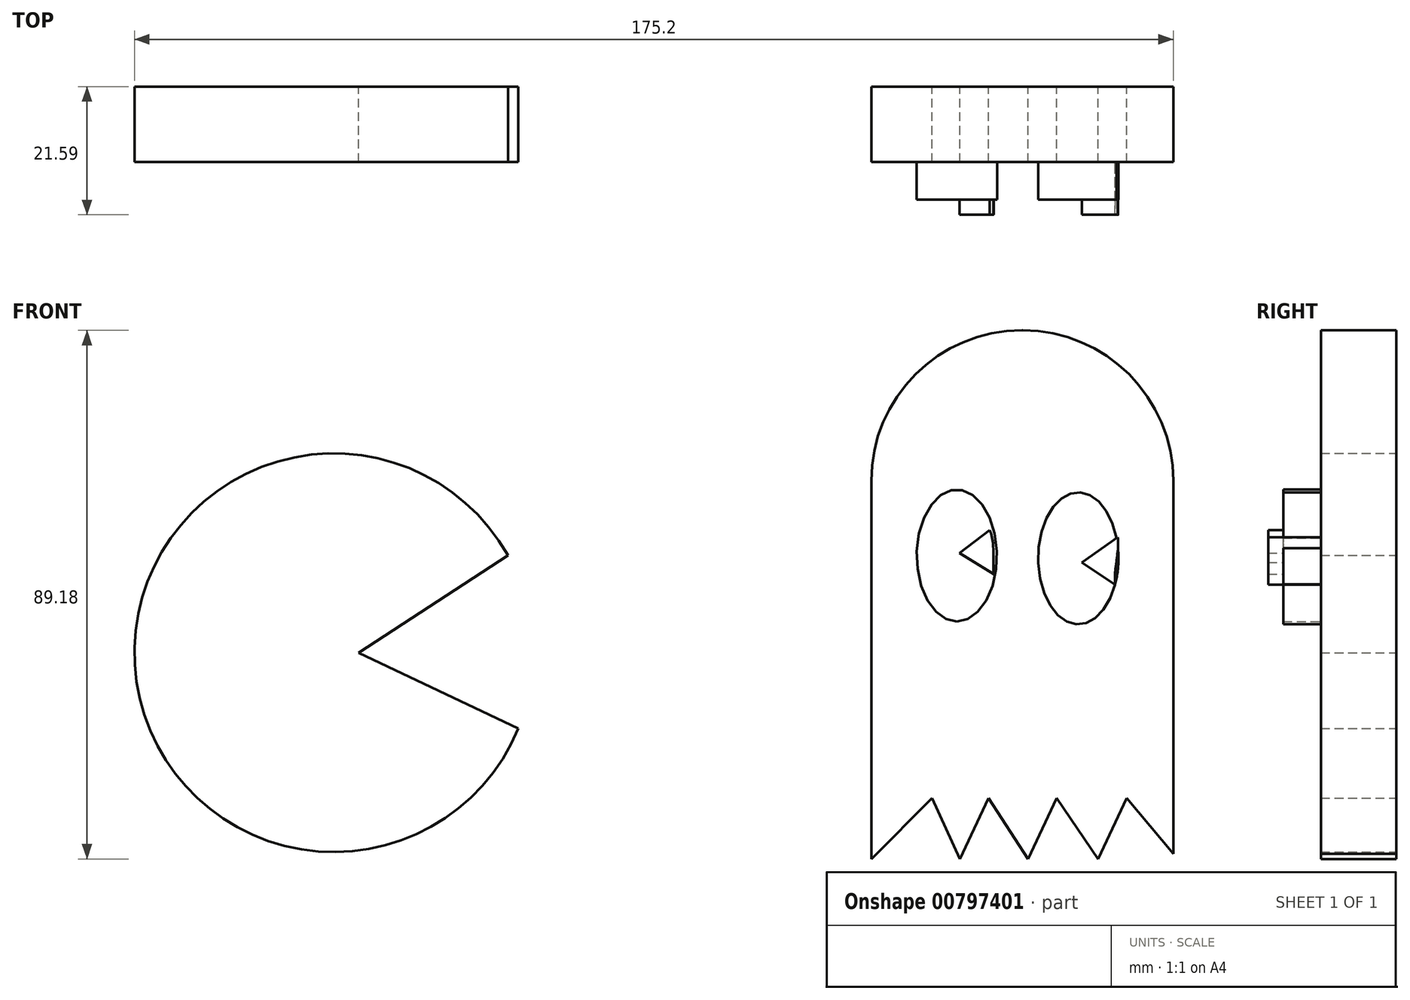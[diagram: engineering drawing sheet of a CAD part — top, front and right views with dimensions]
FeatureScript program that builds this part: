
annotation { "Feature Type Name" : "Feature", "Feature Type Description" : "" }
export const myFeature = defineFeature(function(context is Context, id is Id, definition is map)
    precondition{}
    {
        {
            var Q0;
            Q0=qCreatedBy(makeId("Front.planeOp"),FACE);
            var sketch = newSketch(context, id + "F0", { "sketchPlane" : qUnion([Q0])});
            skArc(sketch, "E0", {"start": v(-31.48, 14.91) * mm, "mid": v(-94.4, -3.54) * mm, "end": v(-29.71, -14.25) * mm});
            skLineSegment(sketch, "E1", {"start": v(-56.67, -1.5) * mm, "end": v(-31.48, 14.91) * mm});
            skLineSegment(sketch, "E2", {"start": v(-56.67, -1.5) * mm, "end": v(-29.71, -14.25) * mm});
            skLineSegment(sketch, "E3.bottom", {"start": v(55.2, 52.9) * mm, "end": v(55.34, 52.9) * mm});
            skLineSegment(sketch, "E3.left", {"start": v(29.8, 27.5) * mm, "end": v(29.8, -36.3) * mm});
            skLineSegment(sketch, "E3.right", {"start": v(80.74, 27.5) * mm, "end": v(80.74, -35.4) * mm});
            skPoint(sketch, "E4.visualSharp", {"position": v(29.8, 52.9) * mm});
            skArc(sketch, "E4.filletArc", {"start": v(33.93, 45.69) * mm, "mid": v(32.81, 44.12) * mm, "end": v(31.86, 42.45) * mm});
            skArc(sketch, "E5.filletArc", {"start": v(55.2, 52.9) * mm, "mid": v(37.24, 45.45) * mm, "end": v(29.8, 27.5) * mm});
            skPoint(sketch, "E6.visualSharp", {"position": v(80.74, 52.9) * mm});
            skArc(sketch, "E6.filletArc", {"start": v(72.07, 49.81) * mm, "mid": v(65.94, 52.4) * mm, "end": v(59.3, 52.74) * mm});
            skArc(sketch, "E7.filletArc", {"start": v(80.74, 27.5) * mm, "mid": v(73.3, 45.45) * mm, "end": v(55.34, 52.9) * mm});
            skLineSegment(sketch, "E8", {"start": v(29.8, -35.4) * mm, "end": v(29.8, -36.3) * mm});
            skLineSegment(sketch, "E9", {"start": v(80.74, -35.4) * mm, "end": v(80.74, -35.4) * mm});
            skLineSegment(sketch, "E10", {"start": v(29.8, -36.3) * mm, "end": v(40.03, -26.06) * mm});
            skLineSegment(sketch, "E11", {"start": v(40.03, -26.06) * mm, "end": v(44.74, -36.3) * mm});
            skLineSegment(sketch, "E12", {"start": v(44.74, -36.3) * mm, "end": v(49.58, -26.06) * mm});
            skLineSegment(sketch, "E13", {"start": v(49.58, -26.06) * mm, "end": v(56.25, -36.3) * mm});
            skLineSegment(sketch, "E14", {"start": v(56.25, -36.3) * mm, "end": v(61.1, -26.06) * mm});
            skLineSegment(sketch, "E15", {"start": v(61.1, -26.06) * mm, "end": v(68.06, -36.3) * mm});
            skLineSegment(sketch, "E16", {"start": v(68.06, -36.3) * mm, "end": v(72.9, -26.06) * mm});
            skLineSegment(sketch, "E17", {"start": v(72.9, -26.06) * mm, "end": v(80.74, -35.4) * mm});
            skSolve(sketch);
        }
        {
            var Q0;
            Q0 = qSketchRegion(id + "F0", true);
            extrude(context, id + "F1", {"entities" : qUnion([Q0]), "depth" : 12.7 * mm, "offsetDistance" : 25.4 * mm});
        }
        {
            var Q0;
            Q0=qCreatedBy(makeId("Front.planeOp"),FACE);
            var sketch = newSketch(context, id + "F2", { "sketchPlane" : qUnion([Q0])});
            skEllipse(sketch, "E18", {"center": v(44.24, 14.89) * mm, "majorRadius": 11.13 * mm, "minorRadius": 6.77 * mm, "majorAxis": v(0, -1)});
            skEllipse(sketch, "E19", {"center": v(64.71, 14.44) * mm, "majorRadius": 11.13 * mm, "minorRadius": 6.77 * mm, "majorAxis": v(0, -1)});
            skSolve(sketch);
        }
        {
            var Q0;
            Q0 = qSketchRegion(id + "F2", true);
            extrude(context, id + "F3", {"entities" : qUnion([Q0]), "operationType" : NewBodyOperationType.ADD, "depth" : 19.05 * mm, "offsetDistance" : 25.4 * mm});
        }
        {
            var Q0;
            Q0=qCreatedBy(makeId("Front.planeOp"),FACE);
            var sketch = newSketch(context, id + "F4", { "sketchPlane" : qUnion([Q0])});
            skLineSegment(sketch, "E20", {"start": v(49.78, 19.18) * mm, "end": v(44.68, 15.33) * mm});
            skLineSegment(sketch, "E21", {"start": v(44.68, 15.33) * mm, "end": v(50.47, 11.77) * mm});
            skFitSpline(sketch, "E22", {"points": [v(49.78, 19.18) * mm, v(50.47, 11.77) * mm], "startDerivative": vector(2.95, -6.65) * mm, "endDerivative": vector(0.9, -7.12) * mm});
            skLineSegment(sketch, "E23", {"start": v(71.39, 18) * mm, "end": v(65.3, 13.7) * mm});
            skLineSegment(sketch, "E24", {"start": v(65.3, 13.7) * mm, "end": v(70.94, 10) * mm});
            skFitSpline(sketch, "E25", {"points": [v(71.39, 18) * mm, v(70.94, 10) * mm], "startDerivative": vector(0.9, -7.12) * mm, "endDerivative": vector(0.9, -7.12) * mm});
            skSolve(sketch);
        }
        {
            var Q0;
            Q0 = qSketchRegion(id + "F4", true);
            extrude(context, id + "F5", {"entities" : qUnion([Q0]), "operationType" : NewBodyOperationType.ADD, "depth" : 21.59 * mm, "offsetDistance" : 25.4 * mm});
        }
    });
